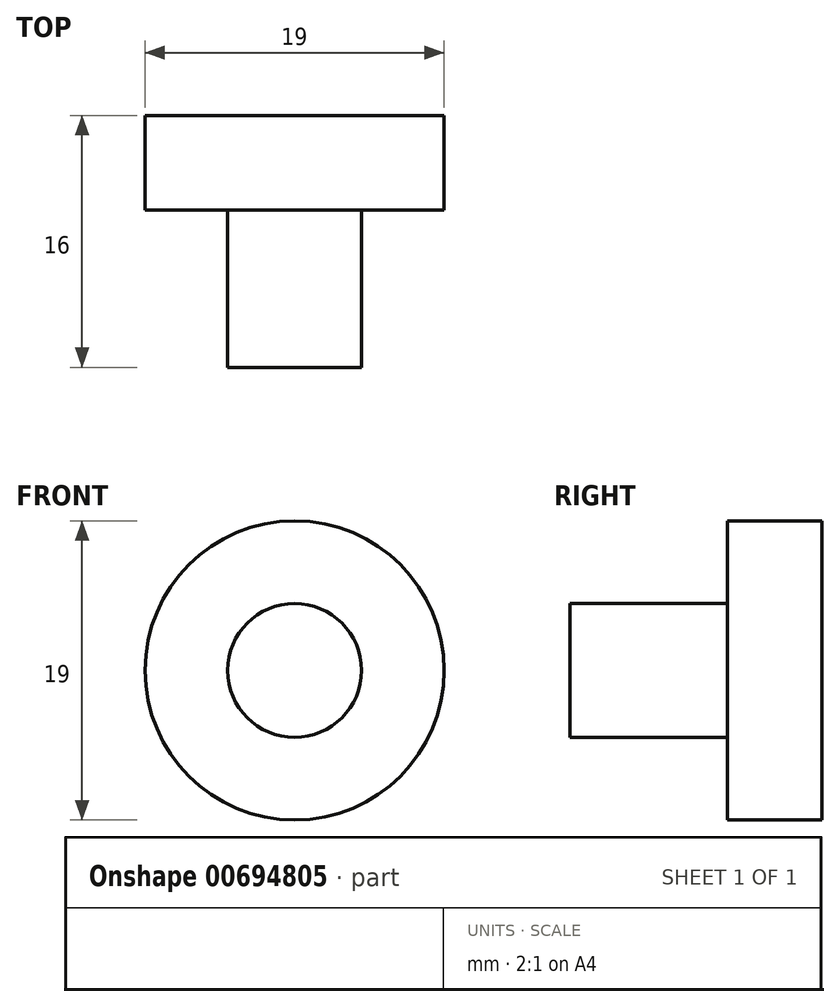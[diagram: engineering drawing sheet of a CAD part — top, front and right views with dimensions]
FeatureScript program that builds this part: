
annotation { "Feature Type Name" : "Feature", "Feature Type Description" : "" }
export const myFeature = defineFeature(function(context is Context, id is Id, definition is map)
    precondition{}
    {
        {
            var Q0;
            Q0=qCreatedBy(makeId("Front.planeOp"),FACE);
            var sketch = newSketch(context, id + "F0", { "sketchPlane" : qUnion([Q0])});
            skCircle(sketch, "E0", {"center": v(0, 0) * mm, "radius": 4.25 * mm});
            skSolve(sketch);
        }
        {
            var Q0;
            Q0=makeQuery(id+"F0.imprint","IMPRINT",FACE,{"disambiguationData":[TD([[makeQuery(id+"F0.imprint","IMPRINT",EDGE,{"derivedFrom":sQuery(id+"F0.wireOp",EDGE,"E0")}),1.0]])]});
            extrude(context, id + "F1", {"entities" : qUnion([Q0]), "depth" : 10 * mm, "offsetDistance" : 25 * mm});
        }
        {
            var Q0;
            Q0=makeQuery(id+"F1.opExtrude","CAP_FACE",FACE,{"disambiguationData":[OSD([sQuery(id+"F0.wireOp",EDGE,"E0")])],"isStart":true});
            var sketch = newSketch(context, id + "F2", { "sketchPlane" : qUnion([Q0])});
            skCircle(sketch, "E1", {"center": v(0, 0) * mm, "radius": 9.5 * mm});
            skSolve(sketch);
        }
        {
            var Q0;
            Q0=makeQuery(id+"F2.imprint","IMPRINT",FACE,{"disambiguationData":[TD([[makeQuery(id+"F2.imprint","IMPRINT",EDGE,{"derivedFrom":sQuery(id+"F2.wireOp",EDGE,"E1")}),1.0]])]});
            var Q1;
            Q1=makeQuery(id+"F2.imprint","IMPRINT",FACE,{"disambiguationData":[TD([[makeQuery(id+"F2.imprint","IMPRINT",EDGE,{"derivedFrom":makeQuery(id+"F1.opExtrude","CAP_EDGE",EDGE,{"disambiguationData":[OSD([sQuery(id+"F0.wireOp",EDGE,"E0")])],"isStart":true})}),-1.0]])]});
            extrude(context, id + "F3", {"entities" : qUnion([Q0, Q1]), "operationType" : NewBodyOperationType.ADD, "depth" : 6 * mm, "offsetDistance" : 25 * mm});
        }
        {
            var Q0;
            Q0=makeQuery(id+"F3.opExtrude","CAP_FACE",FACE,{"disambiguationData":[OSD([sQuery(id+"F2.wireOp",EDGE,"E1")])],"isStart":false});
            var sketch = newSketch(context, id + "F4", { "sketchPlane" : qUnion([Q0])});
            skCircle(sketch, "E2", {"center": v(0, 0) * mm, "radius": 6.5 * mm});
            skSolve(sketch);
        }
        {
            var Q0;
            Q0=sQuery(id+"F4.wireOp",EDGE,"E2");
            extrude(context, id + "F5", {"bodyType" : ToolBodyType.SURFACE, "surfaceEntities" : qUnion([Q0]), "depth" : 200 * mm, "offsetDistance" : 25 * mm});
        }
    });
